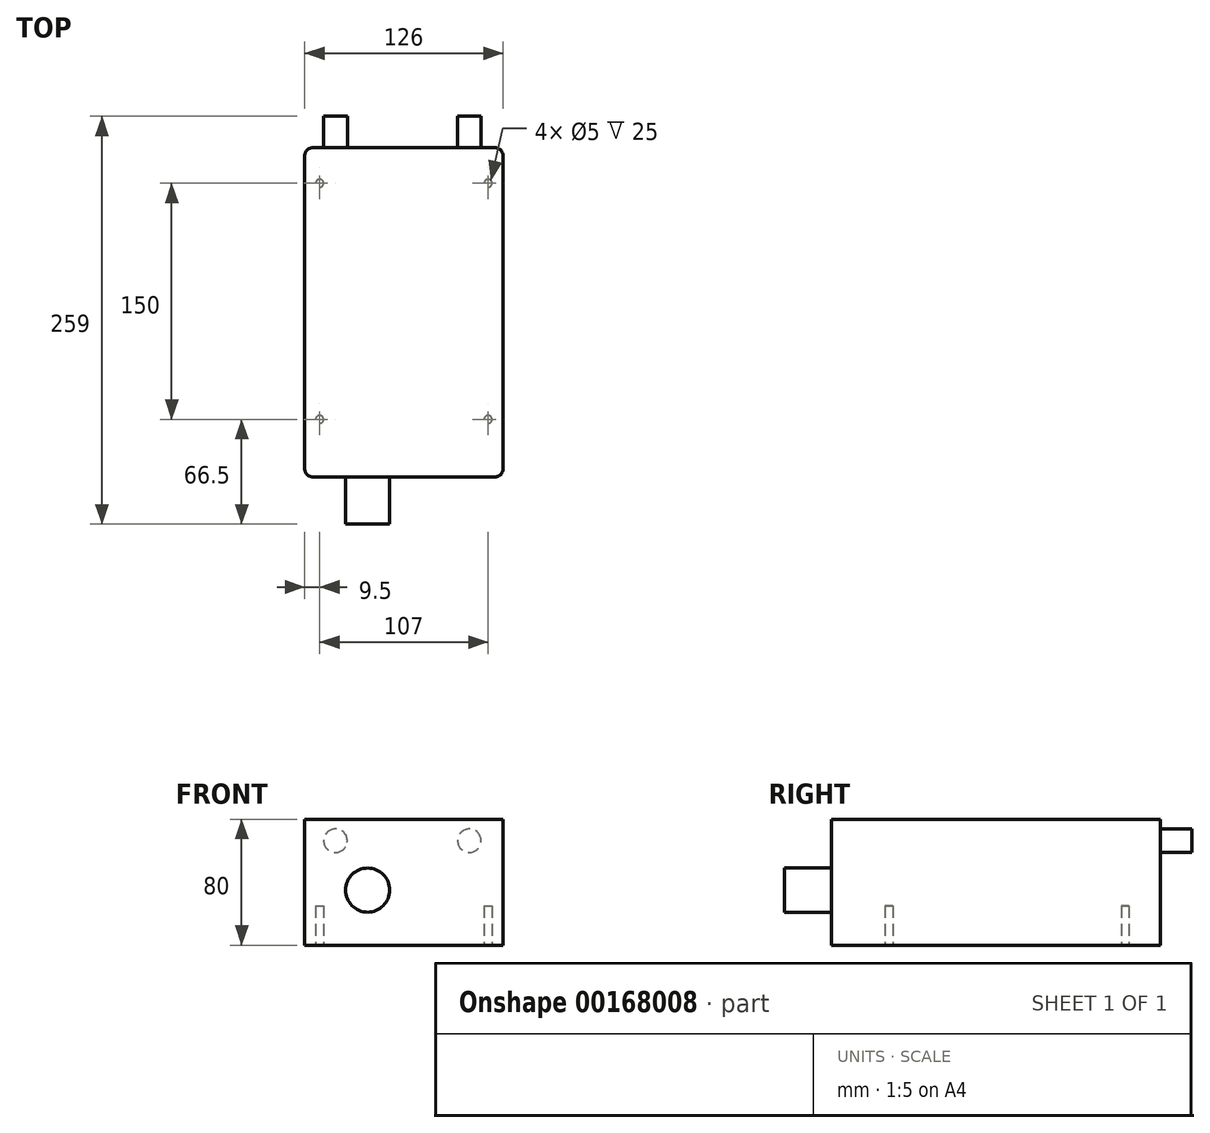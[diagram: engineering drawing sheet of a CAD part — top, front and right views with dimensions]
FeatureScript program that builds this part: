
annotation { "Feature Type Name" : "Feature", "Feature Type Description" : "" }
export const myFeature = defineFeature(function(context is Context, id is Id, definition is map)
    precondition{}
    {
        {
            var Q0;
            Q0=qCreatedBy(makeId("Top.planeOp"),FACE);
            var sketch = newSketch(context, id + "F0", { "sketchPlane" : qUnion([Q0])});
            skLineSegment(sketch, "E0.bottom", {"start": v(58, -104.5) * mm, "end": v(-58, -104.5) * mm});
            skLineSegment(sketch, "E0.top", {"start": v(58, 104.5) * mm, "end": v(-58, 104.5) * mm});
            skLineSegment(sketch, "E0.left", {"start": v(63, -99.5) * mm, "end": v(63, 99.5) * mm});
            skLineSegment(sketch, "E0.right", {"start": v(-63, -99.5) * mm, "end": v(-63, 99.5) * mm});
            skPoint(sketch, "E0.middle", {"position": v(0, 0) * mm});
            skPoint(sketch, "E1.visualSharp", {"position": v(-63, 104.5) * mm});
            skArc(sketch, "E1.filletArc", {"start": v(-58, 104.5) * mm, "mid": v(-61.54, 103.04) * mm, "end": v(-63, 99.5) * mm});
            skPoint(sketch, "E2.visualSharp", {"position": v(63, 104.5) * mm});
            skArc(sketch, "E2.filletArc", {"start": v(63, 99.5) * mm, "mid": v(61.54, 103.04) * mm, "end": v(58, 104.5) * mm});
            skPoint(sketch, "E3.visualSharp", {"position": v(63, -104.5) * mm});
            skArc(sketch, "E3.filletArc", {"start": v(58, -104.5) * mm, "mid": v(61.54, -103.04) * mm, "end": v(63, -99.5) * mm});
            skPoint(sketch, "E4.visualSharp", {"position": v(-63, -104.5) * mm});
            skArc(sketch, "E4.filletArc", {"start": v(-63, -99.5) * mm, "mid": v(-61.54, -103.04) * mm, "end": v(-58, -104.5) * mm});
            skSolve(sketch);
        }
        {
            var Q0;
            Q0=qSketchRegion(id+"F0",true);
            extrude(context, id + "F1", {"entities" : qUnion([Q0]), "depth" : 80 * mm, "symmetric" : true});
        }
        {
            var Q0;
            Q0=makeQuery(id+"F1.opExtrude","CAP_FACE",FACE,{"disambiguationData":[OSD([sQuery(id+"F0.wireOp",EDGE,"E0.bottom"),sQuery(id+"F0.wireOp",EDGE,"E0.top"),sQuery(id+"F0.wireOp",EDGE,"E0.left"),sQuery(id+"F0.wireOp",EDGE,"E0.right"),sQuery(id+"F0.wireOp",EDGE,"E1.filletArc"),sQuery(id+"F0.wireOp",EDGE,"E2.filletArc"),sQuery(id+"F0.wireOp",EDGE,"E3.filletArc"),sQuery(id+"F0.wireOp",EDGE,"E4.filletArc")])],"isStart":true});
            var sketch = newSketch(context, id + "F2", { "sketchPlane" : qUnion([Q0])});
            skCircle(sketch, "E5", {"center": v(-53.5, -82) * mm, "radius": 2.5 * mm});
            skCircle(sketch, "E6.MirrorC", {"center": v(53.5, -82) * mm, "radius": 2.5 * mm});
            skCircle(sketch, "E7.MirrorC", {"center": v(-53.5, 68) * mm, "radius": 2.5 * mm});
            skCircle(sketch, "E8.MirrorC", {"center": v(53.5, 68) * mm, "radius": 2.5 * mm});
            skSolve(sketch);
        }
        {
            var Q0;
            Q0=qSketchRegion(id+"F2",true);
            extrude(context, id + "F3", {"entities" : qUnion([Q0]), "operationType" : NewBodyOperationType.REMOVE, "oppositeDirection" : true, "depth" : 25 * mm});
        }
        {
            var Q0;
            Q0=makeQuery(id+"F1.opExtrude","SWEPT_FACE",FACE,{"disambiguationData":[OSD([sQuery(id+"F0.wireOp",EDGE,"E0.bottom")])]});
            var sketch = newSketch(context, id + "F4", { "sketchPlane" : qUnion([Q0])});
            skCircle(sketch, "E9", {"center": v(-23, -5) * mm, "radius": 14 * mm});
            skSolve(sketch);
        }
        {
            var Q0;
            Q0 = qSketchRegion(id + "F4", true);
            extrude(context, id + "F5", {"entities" : qUnion([Q0]), "operationType" : NewBodyOperationType.ADD, "depth" : 30 * mm});
        }
        {
            var Q0;
            Q0=makeQuery(id+"F1.opExtrude","SWEPT_FACE",FACE,{"disambiguationData":[OSD([sQuery(id+"F0.wireOp",EDGE,"E0.top")])]});
            var sketch = newSketch(context, id + "F6", { "sketchPlane" : qUnion([Q0])});
            skCircle(sketch, "E10", {"center": v(-41.6, 26.34) * mm, "radius": 7.5 * mm});
            skCircle(sketch, "E11", {"center": v(43.45, 26.34) * mm, "radius": 7.5 * mm});
            skSolve(sketch);
        }
        {
            var Q0;
            Q0 = qSketchRegion(id + "F6", true);
            extrude(context, id + "F7", {"entities" : qUnion([Q0]), "operationType" : NewBodyOperationType.ADD, "depth" : 20 * mm});
        }
    });
